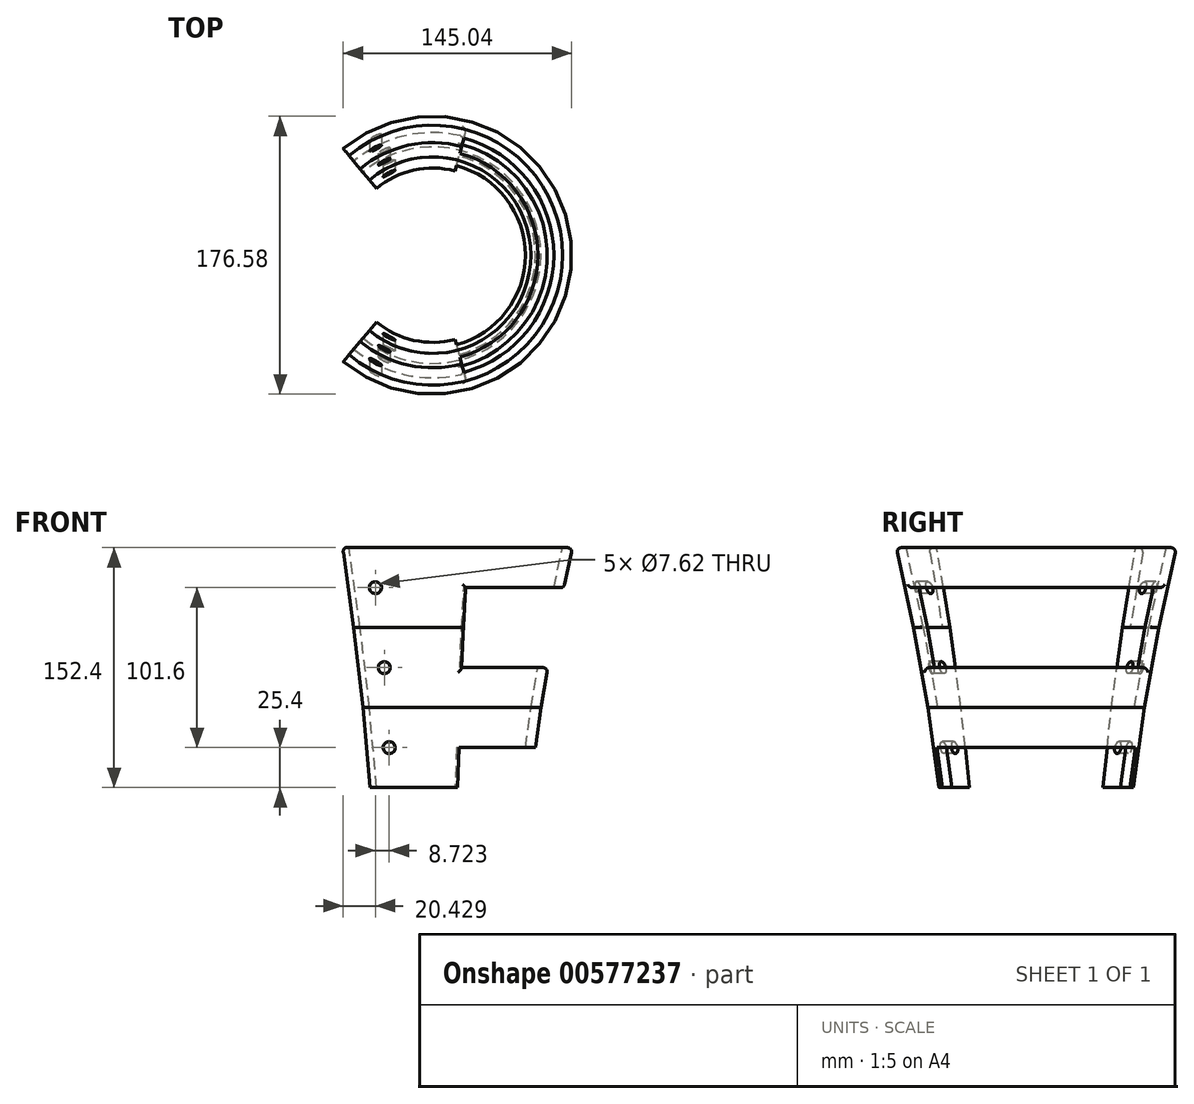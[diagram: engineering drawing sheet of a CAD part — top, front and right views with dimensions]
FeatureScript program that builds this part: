
annotation { "Feature Type Name" : "Feature", "Feature Type Description" : "" }
export const myFeature = defineFeature(function(context is Context, id is Id, definition is map)
    precondition{}
    {
        {
            var Q0;
            Q0=qCreatedBy(makeId("Front.planeOp"),FACE);
            var sketch = newSketch(context, id + "F0", { "sketchPlane" : qUnion([Q0])});
            skLineSegment(sketch, "E0", {"start": v(0, 0) * mm, "end": v(0, 50.8) * mm});
            skLineSegment(sketch, "E1", {"start": v(0, 50.8) * mm, "end": v(68.76, 50.8) * mm, "construction": true});
            skLineSegment(sketch, "E2", {"start": v(0, 0) * mm, "end": v(61.72, 0) * mm});
            skLineSegment(sketch, "E3", {"start": v(61.72, 0) * mm, "end": v(68.76, 50.8) * mm});
            skLineSegment(sketch, "E4", {"start": v(0, 50.8) * mm, "end": v(0, 101.6) * mm});
            skLineSegment(sketch, "E5", {"start": v(0, 101.6) * mm, "end": v(77.84, 101.6) * mm, "construction": true});
            skLineSegment(sketch, "E6", {"start": v(77.84, 101.6) * mm, "end": v(68.76, 50.8) * mm});
            skLineSegment(sketch, "E7", {"start": v(0, 101.6) * mm, "end": v(0, 152.4) * mm});
            skLineSegment(sketch, "E8", {"start": v(0, 152.4) * mm, "end": v(88.9, 152.4) * mm});
            skLineSegment(sketch, "E9", {"start": v(88.9, 152.4) * mm, "end": v(77.84, 101.6) * mm});
            skSolve(sketch);
        }
        {
            var Q0;
            Q0=qSketchRegion(id+"F0",true);
            var Q1;
            Q1=sQuery(id+"F0.wireOp",EDGE,"E7");
            revolve(context, id + "F1", {"entities" : qUnion([Q0]), "axis" : qUnion([Q1]), "revolveType" : RevolveType.SYMMETRIC, "angle" : 260 * degree});
        }
        {
            var Q0;
            Q0=qCreatedBy(makeId("Front.planeOp"),FACE);
            var sketch = newSketch(context, id + "F2", { "sketchPlane" : qUnion([Q0])});
            skLineSegment(sketch, "E10", {"start": v(0, 50.8) * mm, "end": v(62.4, 50.8) * mm, "construction": true});
            skLineSegment(sketch, "E11", {"start": v(0, 50.8) * mm, "end": v(0, 101.6) * mm});
            skLineSegment(sketch, "E12", {"start": v(0, 101.6) * mm, "end": v(71.49, 101.6) * mm, "construction": true});
            skLineSegment(sketch, "E13", {"start": v(71.49, 101.6) * mm, "end": v(62.4, 50.8) * mm});
            skLineSegment(sketch, "E14", {"start": v(0, 101.6) * mm, "end": v(0, 152.4) * mm});
            skLineSegment(sketch, "E15", {"start": v(0, 152.4) * mm, "end": v(82.55, 152.4) * mm});
            skLineSegment(sketch, "E16", {"start": v(82.55, 152.4) * mm, "end": v(71.49, 101.6) * mm});
            skPoint(sketch, "E17.start.orphan", {"position": v(1.44, 0) * mm});
            skLineSegment(sketch, "E18", {"start": v(0, 50.8) * mm, "end": v(0, 0) * mm});
            skLineSegment(sketch, "E19", {"start": v(0, 0) * mm, "end": v(55.37, 0) * mm});
            skLineSegment(sketch, "E20", {"start": v(55.37, 0) * mm, "end": v(62.4, 50.8) * mm});
            skSolve(sketch);
        }
        {
            var Q0;
            Q0=makeQuery(id+"F0.imprint","IMPRINT",FACE,{"disambiguationData":[TD([[makeQuery(id+"F0.imprint","IMPRINT",EDGE,{"derivedFrom":sQuery(id+"F0.wireOp",EDGE,"E0")}),-1.0]])]});
            var Q1;
            Q1=sQuery(id+"F2.wireOp",EDGE,"E11");
            revolve(context, id + "F3", {"operationType" : NewBodyOperationType.ADD, "entities" : qUnion([Q0]), "axis" : qUnion([Q1]), "revolveType" : RevolveType.ONE_DIRECTION, "oppositeDirection" : true, "angle" : 30 * degree});
        }
        {
            var Q0;
            Q0=qSketchRegion(id+"F2",true);
            var Q1;
            Q1 = qSketchRegion(id + "F7", true);
            var Q2;
            Q2=sQuery(id+"F2.wireOp",EDGE,"E14");
            revolve(context, id + "F4", {"operationType" : NewBodyOperationType.REMOVE, "entities" : qUnion([Q0, Q1]), "axis" : qUnion([Q2]), "revolveType" : RevolveType.FULL, "oppositeDirection" : true});
        }
        {
            var Q0;
            Q0=qCreatedBy(makeId("Front.planeOp"),FACE);
            var sketch = newSketch(context, id + "F5", { "sketchPlane" : qUnion([Q0])});
            skLineSegment(sketch, "E21", {"start": v(0, 0) * mm, "end": v(0, 50.8) * mm, "construction": true});
            skLineSegment(sketch, "E22", {"start": v(0, 50.8) * mm, "end": v(0, 101.6) * mm, "construction": true});
            skLineSegment(sketch, "E23", {"start": v(0, 101.6) * mm, "end": v(0, 152.4) * mm, "construction": true});
            skLineSegment(sketch, "E24", {"start": v(0, 127) * mm, "end": v(-20.79, 127) * mm, "construction": true});
            skPoint(sketch, "E24.endSnap0", {"position": v(0, 127) * mm});
            skLineSegment(sketch, "E25", {"start": v(0, 50.8) * mm, "end": v(0, 76.2) * mm, "construction": true});
            skLineSegment(sketch, "E26", {"start": v(0, 76.2) * mm, "end": v(-17.23, 76.2) * mm, "construction": true});
            skLineSegment(sketch, "E27", {"start": v(0, 0) * mm, "end": v(0, 25.4) * mm, "construction": true});
            skLineSegment(sketch, "E28", {"start": v(0, 25.4) * mm, "end": v(-15.45, 25.4) * mm, "construction": true});
            skLineSegment(sketch, "E29", {"start": v(-20.79, 127) * mm, "end": v(-36.32, 127) * mm, "construction": true});
            skLineSegment(sketch, "E30", {"start": v(-17.23, 76.2) * mm, "end": v(-30.67, 76.2) * mm, "construction": true});
            skLineSegment(sketch, "E31", {"start": v(-15.45, 25.4) * mm, "end": v(-27.6, 25.4) * mm, "construction": true});
            skCircle(sketch, "E32", {"center": v(-36.32, 127) * mm, "radius": 3.81 * mm});
            skCircle(sketch, "E33", {"center": v(-30.67, 76.2) * mm, "radius": 3.81 * mm});
            skCircle(sketch, "E34", {"center": v(-27.6, 25.4) * mm, "radius": 3.81 * mm});
            skSolve(sketch);
        }
        {
            var Q0;
            Q0=qSketchRegion(id+"F5",true);
            var Q1;
            Q1 = qSketchRegion(id + "F7", true);
            extrude(context, id + "F6", {"entities" : qUnion([Q0, Q1]), "operationType" : NewBodyOperationType.REMOVE, "endBound" : BoundingType.SYMMETRIC, "oppositeDirection" : true, "depth" : 249.43 * mm, "offsetDistance" : 25.4 * mm});
        }
        {
            var Q0;
            Q0=qCreatedBy(makeId("Front.planeOp"),FACE);
            var sketch = newSketch(context, id + "F7", { "sketchPlane" : qUnion([Q0])});
            skLineSegment(sketch, "E35", {"start": v(55.37, 0) * mm, "end": v(61.72, 0) * mm});
            skLineSegment(sketch, "E36", {"start": v(0, 0) * mm, "end": v(0, 50.8) * mm, "construction": true});
            skLineSegment(sketch, "E37", {"start": v(0, 50.8) * mm, "end": v(0, 101.6) * mm, "construction": true});
            skLineSegment(sketch, "E38", {"start": v(0, 101.6) * mm, "end": v(0, 152.4) * mm, "construction": true});
            skLineSegment(sketch, "E39", {"start": v(82.55, 152.4) * mm, "end": v(88.9, 152.4) * mm});
            skLineSegment(sketch, "E40", {"start": v(77.85, 101.6) * mm, "end": v(83.38, 127) * mm});
            skLineSegment(sketch, "E41", {"start": v(61.72, 0) * mm, "end": v(65.24, 25.4) * mm});
            skLineSegment(sketch, "E42", {"start": v(58.89, 25.4) * mm, "end": v(55.37, 0) * mm});
            skLineSegment(sketch, "E43", {"start": v(0, 0) * mm, "end": v(61.72, 0) * mm, "construction": true});
            skLineSegment(sketch, "E44", {"start": v(0, 50.8) * mm, "end": v(62.4, 50.8) * mm, "construction": true});
            skLineSegment(sketch, "E45", {"start": v(0, 101.6) * mm, "end": v(71.5, 101.6) * mm, "construction": true});
            skLineSegment(sketch, "E46", {"start": v(0, 152.4) * mm, "end": v(82.55, 152.4) * mm, "construction": true});
            skLineSegment(sketch, "E47", {"start": v(0, 0) * mm, "end": v(0, 25.4) * mm, "construction": true});
            skLineSegment(sketch, "E48", {"start": v(0, 25.4) * mm, "end": v(65.24, 25.4) * mm, "construction": true});
            skLineSegment(sketch, "E49", {"start": v(58.89, 25.4) * mm, "end": v(65.24, 25.4) * mm});
            skLineSegment(sketch, "E50", {"start": v(0, 50.8) * mm, "end": v(0, 76.2) * mm, "construction": true});
            skLineSegment(sketch, "E51", {"start": v(0, 76.2) * mm, "end": v(0, 127) * mm, "construction": true});
            skLineSegment(sketch, "E52", {"start": v(0, 127) * mm, "end": v(77.03, 127) * mm, "construction": true});
            skLineSegment(sketch, "E53", {"start": v(0, 76.2) * mm, "end": v(66.95, 76.2) * mm, "construction": true});
            skLineSegment(sketch, "E54", {"start": v(77.03, 127) * mm, "end": v(83.38, 127) * mm});
            skLineSegment(sketch, "E55", {"start": v(77.85, 101.6) * mm, "end": v(73.3, 76.2) * mm});
            skPoint(sketch, "E56.start.orphan", {"position": v(68.76, 50.8) * mm});
            skLineSegment(sketch, "E57", {"start": v(73.3, 76.2) * mm, "end": v(66.45, 76.2) * mm});
            skLineSegment(sketch, "E58", {"start": v(83.38, 127) * mm, "end": v(76.52, 127) * mm});
            skLineSegment(sketch, "E59", {"start": v(77.85, 101.6) * mm, "end": v(71, 101.6) * mm, "construction": true});
            skLineSegment(sketch, "E60", {"start": v(71, 101.6) * mm, "end": v(76.52, 127) * mm});
            skLineSegment(sketch, "E61", {"start": v(71, 101.6) * mm, "end": v(66.45, 76.2) * mm});
            skSolve(sketch);
        }
        {
            var Q0;
            Q0 = qSketchRegion(id + "F7", true);
            var Q1;
            Q1=sQuery(id+"F7.wireOp",EDGE,"E38");
            revolve(context, id + "F8", {"operationType" : NewBodyOperationType.REMOVE, "entities" : qUnion([Q0]), "axis" : qUnion([Q1]), "revolveType" : RevolveType.SYMMETRIC, "oppositeDirection" : true, "angle" : 150 * degree});
        }
        {
            var Q0;
            Q0=makeQuery(id+"F8.boolean.opBoolean","INTERSECT",EDGE,{"derivedFrom":[makeQuery(id+"F1.opRevolve","SWEPT_FACE",FACE,{"disambiguationData":[OSD([sQuery(id+"F0.wireOp",EDGE,"E9")])]}),makeQuery(id+"F8.opRevolve","SWEPT_FACE",FACE,{"disambiguationData":[OSD([sQuery(id+"F7.wireOp",EDGE,"E58")])]})]});
            var Q1;
            Q1=makeQuery(id+"F8.boolean.opBoolean","INTERSECT",EDGE,{"derivedFrom":[makeQuery(id+"F1.opRevolve","SWEPT_FACE",FACE,{"disambiguationData":[OSD([sQuery(id+"F0.wireOp",EDGE,"E9")])]}),makeQuery(id+"F8.opRevolve","CAP_FACE",FACE,{"disambiguationData":[OSD([sQuery(id+"F7.wireOp",EDGE,"E40"),sQuery(id+"F7.wireOp",EDGE,"E55"),sQuery(id+"F7.wireOp",EDGE,"E57"),sQuery(id+"F7.wireOp",EDGE,"E58"),sQuery(id+"F7.wireOp",EDGE,"E60"),sQuery(id+"F7.wireOp",EDGE,"E61")])],"isStart":false})]});
            var Q2;
            Q2=makeQuery(id+"F8.boolean.opBoolean","INTERSECT",EDGE,{"derivedFrom":[makeQuery(id+"F1.opRevolve","SWEPT_FACE",FACE,{"disambiguationData":[OSD([sQuery(id+"F0.wireOp",EDGE,"E9")])]}),makeQuery(id+"F8.opRevolve","CAP_FACE",FACE,{"disambiguationData":[OSD([sQuery(id+"F7.wireOp",EDGE,"E40"),sQuery(id+"F7.wireOp",EDGE,"E55"),sQuery(id+"F7.wireOp",EDGE,"E57"),sQuery(id+"F7.wireOp",EDGE,"E58"),sQuery(id+"F7.wireOp",EDGE,"E60"),sQuery(id+"F7.wireOp",EDGE,"E61")])],"isStart":true})]});
            var Q3;
            Q3=makeQuery(id+"F8.boolean.opBoolean","INTERSECT",EDGE,{"derivedFrom":[makeQuery(id+"F1.opRevolve","SWEPT_FACE",FACE,{"disambiguationData":[OSD([sQuery(id+"F0.wireOp",EDGE,"E6")])]}),makeQuery(id+"F8.opRevolve","SWEPT_FACE",FACE,{"disambiguationData":[OSD([sQuery(id+"F7.wireOp",EDGE,"E57")])]})]});
            var Q4;
            Q4=makeQuery(id+"F8.boolean.opBoolean","COPY",EDGE,{"derivedFrom":makeQuery(id+"F8.opRevolve","SWEPT_EDGE",EDGE,{"disambiguationData":[OSD([sQuery(id+"F7.wireOp",EDGE,"E41"),sQuery(id+"F7.wireOp",EDGE,"E49")])]})});
            var Q5;
            Q5=makeQuery(id+"F8.boolean.opBoolean","COPY",EDGE,{"derivedFrom":makeQuery(id+"F8.opRevolve","CAP_EDGE",EDGE,{"disambiguationData":[OSD([sQuery(id+"F7.wireOp",EDGE,"E41")])],"isStart":false})});
            var Q6;
            Q6=makeQuery(id+"F8.boolean.opBoolean","COPY",EDGE,{"derivedFrom":makeQuery(id+"F8.opRevolve","CAP_EDGE",EDGE,{"disambiguationData":[OSD([sQuery(id+"F7.wireOp",EDGE,"E41")])],"isStart":true})});
            var Q7;
            Q7=makeQuery(id+"F1.opRevolve","SWEPT_EDGE",EDGE,{"disambiguationData":[OSD([sQuery(id+"F0.wireOp",EDGE,"E8"),sQuery(id+"F0.wireOp",EDGE,"E9")])]});
            fillet(context, id + "F9", {"entities" : qUnion([Q0, Q1, Q2, Q3, Q4, Q5, Q6, Q7]), "radius" : 2.54 * mm, "tangentPropagation" : true, "allowEdgeOverflow" : false});
        }
    });
